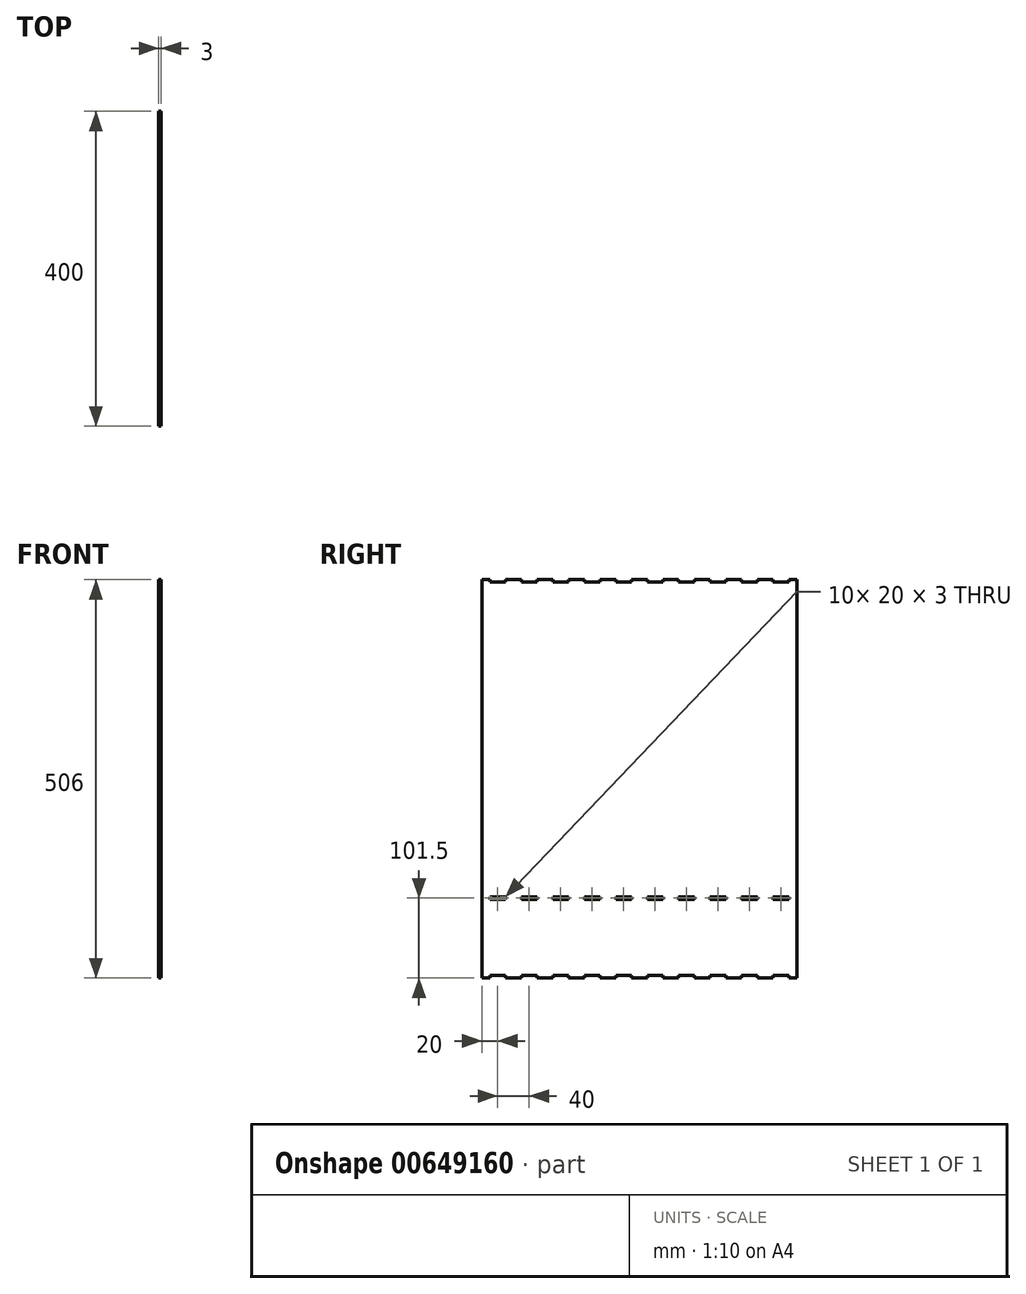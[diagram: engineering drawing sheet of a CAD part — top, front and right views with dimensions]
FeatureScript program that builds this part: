
annotation { "Feature Type Name" : "Feature", "Feature Type Description" : "" }
export const myFeature = defineFeature(function(context is Context, id is Id, definition is map)
    precondition{}
    {
        {
            var Q0;
            Q0=qCreatedBy(makeId("Right.planeOp"),FACE);
            var sketch = newSketch(context, id + "F0", { "sketchPlane" : qUnion([Q0])});
            skLineSegment(sketch, "E0.bottom", {"start": v(200, 250) * mm, "end": v(-200, 250) * mm});
            skLineSegment(sketch, "E0.top", {"start": v(200, -250) * mm, "end": v(-200, -250) * mm});
            skLineSegment(sketch, "E0.left", {"start": v(200, 250) * mm, "end": v(200, -250) * mm});
            skLineSegment(sketch, "E0.right", {"start": v(-200, 250) * mm, "end": v(-200, -250) * mm});
            skPoint(sketch, "E0.middle", {"position": v(0, 0) * mm});
            skSolve(sketch);
        }
        {
            var Q0;
            Q0=qSketchRegion(id+"F0",true);
            extrude(context, id + "F1", {"entities" : qUnion([Q0]), "depth" : 3 * mm, "offsetDistance" : 25 * mm});
        }
        {
            var Q0;
            Q0=makeQuery(id+"F1.opExtrude","CAP_FACE",FACE,{"disambiguationData":[OSD([sQuery(id+"F0.wireOp",EDGE,"E0.bottom"),sQuery(id+"F0.wireOp",EDGE,"E0.top"),sQuery(id+"F0.wireOp",EDGE,"E0.left"),sQuery(id+"F0.wireOp",EDGE,"E0.right")])],"isStart":false});
            var sketch = newSketch(context, id + "F2", { "sketchPlane" : qUnion([Q0])});
            skLineSegment(sketch, "E1.bottom", {"start": v(-200, 250) * mm, "end": v(-190, 250) * mm});
            skLineSegment(sketch, "E1.top", {"start": v(-200, 253) * mm, "end": v(-190, 253) * mm});
            skLineSegment(sketch, "E1.left", {"start": v(-200, 250) * mm, "end": v(-200, 253) * mm});
            skLineSegment(sketch, "E1.right", {"start": v(-190, 250) * mm, "end": v(-190, 253) * mm});
            skLineSegment(sketch, "E2", {"start": v(-190, 250) * mm, "end": v(-170, 250) * mm, "construction": true});
            skLineSegment(sketch, "E3.bottom", {"start": v(-170, 250) * mm, "end": v(-150, 250) * mm});
            skLineSegment(sketch, "E3.top", {"start": v(-170, 253) * mm, "end": v(-150, 253) * mm});
            skLineSegment(sketch, "E3.left", {"start": v(-170, 250) * mm, "end": v(-170, 253) * mm});
            skLineSegment(sketch, "E3.right", {"start": v(-150, 250) * mm, "end": v(-150, 253) * mm});
            skLineSegment(sketch, "E4.1.0.0", {"start": v(-110, 250) * mm, "end": v(-110, 253) * mm});
            skLineSegment(sketch, "E4.1.0.1", {"start": v(-130, 250) * mm, "end": v(-110, 250) * mm});
            skLineSegment(sketch, "E4.1.0.2", {"start": v(-130, 250) * mm, "end": v(-130, 253) * mm});
            skLineSegment(sketch, "E4.1.0.3", {"start": v(-130, 253) * mm, "end": v(-110, 253) * mm});
            skLineSegment(sketch, "E4.2.0.0", {"start": v(-70, 250) * mm, "end": v(-70, 253) * mm});
            skLineSegment(sketch, "E4.2.0.1", {"start": v(-90, 250) * mm, "end": v(-70, 250) * mm});
            skLineSegment(sketch, "E4.2.0.2", {"start": v(-90, 250) * mm, "end": v(-90, 253) * mm});
            skLineSegment(sketch, "E4.2.0.3", {"start": v(-90, 253) * mm, "end": v(-70, 253) * mm});
            skLineSegment(sketch, "E4.3.0.0", {"start": v(-30, 250) * mm, "end": v(-30, 253) * mm});
            skLineSegment(sketch, "E4.3.0.1", {"start": v(-50, 250) * mm, "end": v(-30, 250) * mm});
            skLineSegment(sketch, "E4.3.0.2", {"start": v(-50, 250) * mm, "end": v(-50, 253) * mm});
            skLineSegment(sketch, "E4.3.0.3", {"start": v(-50, 253) * mm, "end": v(-30, 253) * mm});
            skLineSegment(sketch, "E4.4.0.0", {"start": v(10, 250) * mm, "end": v(10, 253) * mm});
            skLineSegment(sketch, "E4.4.0.1", {"start": v(-10, 250) * mm, "end": v(10, 250) * mm});
            skLineSegment(sketch, "E4.4.0.2", {"start": v(-10, 250) * mm, "end": v(-10, 253) * mm});
            skLineSegment(sketch, "E4.4.0.3", {"start": v(-10, 253) * mm, "end": v(10, 253) * mm});
            skLineSegment(sketch, "E4.5.0.0", {"start": v(50, 250) * mm, "end": v(50, 253) * mm});
            skLineSegment(sketch, "E4.5.0.1", {"start": v(30, 250) * mm, "end": v(50, 250) * mm});
            skLineSegment(sketch, "E4.5.0.2", {"start": v(30, 250) * mm, "end": v(30, 253) * mm});
            skLineSegment(sketch, "E4.5.0.3", {"start": v(30, 253) * mm, "end": v(50, 253) * mm});
            skLineSegment(sketch, "E4.6.0.0", {"start": v(90, 250) * mm, "end": v(90, 253) * mm});
            skLineSegment(sketch, "E4.6.0.1", {"start": v(70, 250) * mm, "end": v(90, 250) * mm});
            skLineSegment(sketch, "E4.6.0.2", {"start": v(70, 250) * mm, "end": v(70, 253) * mm});
            skLineSegment(sketch, "E4.6.0.3", {"start": v(70, 253) * mm, "end": v(90, 253) * mm});
            skLineSegment(sketch, "E4.7.0.0", {"start": v(130, 250) * mm, "end": v(130, 253) * mm});
            skLineSegment(sketch, "E4.7.0.1", {"start": v(110, 250) * mm, "end": v(130, 250) * mm});
            skLineSegment(sketch, "E4.7.0.2", {"start": v(110, 250) * mm, "end": v(110, 253) * mm});
            skLineSegment(sketch, "E4.7.0.3", {"start": v(110, 253) * mm, "end": v(130, 253) * mm});
            skLineSegment(sketch, "E4.8.0.0", {"start": v(170, 250) * mm, "end": v(170, 253) * mm});
            skLineSegment(sketch, "E4.8.0.1", {"start": v(150, 250) * mm, "end": v(170, 250) * mm});
            skLineSegment(sketch, "E4.8.0.2", {"start": v(150, 250) * mm, "end": v(150, 253) * mm});
            skLineSegment(sketch, "E4.8.0.3", {"start": v(150, 253) * mm, "end": v(170, 253) * mm});
            skLineSegment(sketch, "E4.direction1", {"start": v(-170, 250) * mm, "end": v(-130, 250) * mm, "construction": true});
            skLineSegment(sketch, "E5.bottom", {"start": v(200, 250) * mm, "end": v(190, 250) * mm});
            skLineSegment(sketch, "E5.top", {"start": v(200, 253) * mm, "end": v(190, 253) * mm});
            skLineSegment(sketch, "E5.left", {"start": v(200, 250) * mm, "end": v(200, 253) * mm});
            skLineSegment(sketch, "E5.right", {"start": v(190, 250) * mm, "end": v(190, 253) * mm});
            skLineSegment(sketch, "E6.MirrorCS", {"start": v(-110, -250) * mm, "end": v(-110, -253) * mm});
            skLineSegment(sketch, "E7.MirrorCS", {"start": v(-170, -250) * mm, "end": v(-150, -250) * mm});
            skLineSegment(sketch, "E8.MirrorCS", {"start": v(-90, -253) * mm, "end": v(-70, -253) * mm});
            skLineSegment(sketch, "E9.MirrorCS", {"start": v(10, -250) * mm, "end": v(10, -253) * mm});
            skLineSegment(sketch, "E10.MirrorCS", {"start": v(170, -250) * mm, "end": v(170, -253) * mm});
            skLineSegment(sketch, "E11.MirrorCS", {"start": v(90, -250) * mm, "end": v(90, -253) * mm});
            skLineSegment(sketch, "E12.MirrorCS", {"start": v(200, -253) * mm, "end": v(190, -253) * mm});
            skLineSegment(sketch, "E13.MirrorCS", {"start": v(200, -250) * mm, "end": v(190, -250) * mm});
            skLineSegment(sketch, "E14.MirrorCS", {"start": v(-130, -253) * mm, "end": v(-110, -253) * mm});
            skLineSegment(sketch, "E15.MirrorCS", {"start": v(50, -250) * mm, "end": v(50, -253) * mm});
            skLineSegment(sketch, "E16.MirrorCS", {"start": v(-130, -250) * mm, "end": v(-130, -253) * mm});
            skLineSegment(sketch, "E17.MirrorCS", {"start": v(-130, -250) * mm, "end": v(-110, -250) * mm});
            skLineSegment(sketch, "E18.MirrorCS", {"start": v(-150, -250) * mm, "end": v(-150, -253) * mm});
            skLineSegment(sketch, "E19.MirrorCS", {"start": v(-170, -250) * mm, "end": v(-170, -253) * mm});
            skLineSegment(sketch, "E20.MirrorCS", {"start": v(-170, -253) * mm, "end": v(-150, -253) * mm});
            skLineSegment(sketch, "E21.MirrorCS", {"start": v(-190, -250) * mm, "end": v(-170, -250) * mm, "construction": true});
            skLineSegment(sketch, "E22.MirrorCS", {"start": v(-190, -250) * mm, "end": v(-190, -253) * mm});
            skLineSegment(sketch, "E23.MirrorCS", {"start": v(-200, -253) * mm, "end": v(-190, -253) * mm});
            skLineSegment(sketch, "E24.MirrorCS", {"start": v(-200, -250) * mm, "end": v(-190, -250) * mm});
            skLineSegment(sketch, "E25.MirrorCS", {"start": v(-90, -250) * mm, "end": v(-90, -253) * mm});
            skLineSegment(sketch, "E26.MirrorCS", {"start": v(-90, -250) * mm, "end": v(-70, -250) * mm});
            skLineSegment(sketch, "E27.MirrorCS", {"start": v(-70, -250) * mm, "end": v(-70, -253) * mm});
            skLineSegment(sketch, "E28.MirrorCS", {"start": v(-30, -250) * mm, "end": v(-30, -253) * mm});
            skLineSegment(sketch, "E29.MirrorCS", {"start": v(130, -250) * mm, "end": v(130, -253) * mm});
            skLineSegment(sketch, "E30.MirrorCS", {"start": v(-10, -253) * mm, "end": v(10, -253) * mm});
            skLineSegment(sketch, "E31.MirrorCS", {"start": v(150, -253) * mm, "end": v(170, -253) * mm});
            skLineSegment(sketch, "E32.MirrorCS", {"start": v(70, -253) * mm, "end": v(90, -253) * mm});
            skLineSegment(sketch, "E33.MirrorCS", {"start": v(-10, -250) * mm, "end": v(-10, -253) * mm});
            skLineSegment(sketch, "E34.MirrorCS", {"start": v(150, -250) * mm, "end": v(150, -253) * mm});
            skLineSegment(sketch, "E35.MirrorCS", {"start": v(-10, -250) * mm, "end": v(10, -250) * mm});
            skLineSegment(sketch, "E36.MirrorCS", {"start": v(70, -250) * mm, "end": v(70, -253) * mm});
            skLineSegment(sketch, "E37.MirrorCS", {"start": v(150, -250) * mm, "end": v(170, -250) * mm});
            skLineSegment(sketch, "E38.MirrorCS", {"start": v(70, -250) * mm, "end": v(90, -250) * mm});
            skLineSegment(sketch, "E39.MirrorCS", {"start": v(200, -250) * mm, "end": v(200, -253) * mm});
            skLineSegment(sketch, "E40.MirrorCS", {"start": v(190, -250) * mm, "end": v(190, -253) * mm});
            skLineSegment(sketch, "E41.MirrorCS", {"start": v(-50, -253) * mm, "end": v(-30, -253) * mm});
            skLineSegment(sketch, "E42.MirrorCS", {"start": v(110, -253) * mm, "end": v(130, -253) * mm});
            skLineSegment(sketch, "E43.MirrorCS", {"start": v(30, -250) * mm, "end": v(30, -253) * mm});
            skLineSegment(sketch, "E44.MirrorCS", {"start": v(-50, -250) * mm, "end": v(-50, -253) * mm});
            skLineSegment(sketch, "E45.MirrorCS", {"start": v(110, -250) * mm, "end": v(110, -253) * mm});
            skLineSegment(sketch, "E46.MirrorCS", {"start": v(30, -250) * mm, "end": v(50, -250) * mm});
            skLineSegment(sketch, "E47.MirrorCS", {"start": v(-50, -250) * mm, "end": v(-30, -250) * mm});
            skLineSegment(sketch, "E48.MirrorCS", {"start": v(110, -250) * mm, "end": v(130, -250) * mm});
            skLineSegment(sketch, "E49.MirrorCS", {"start": v(-170, -250) * mm, "end": v(-130, -250) * mm, "construction": true});
            skLineSegment(sketch, "E50.MirrorCS", {"start": v(-200, -250) * mm, "end": v(-200, -253) * mm});
            skLineSegment(sketch, "E51.MirrorCS", {"start": v(30, -253) * mm, "end": v(50, -253) * mm});
            skSolve(sketch);
        }
        {
            var Q0;
            Q0=qSketchRegion(id+"F2",true);
            var Q1;
            Q1=makeQuery(id+"F1.opExtrude","CAP_FACE",FACE,{"disambiguationData":[OSD([sQuery(id+"F0.wireOp",EDGE,"E0.bottom"),sQuery(id+"F0.wireOp",EDGE,"E0.top"),sQuery(id+"F0.wireOp",EDGE,"E0.left"),sQuery(id+"F0.wireOp",EDGE,"E0.right")])],"isStart":true});
            extrude(context, id + "F3", {"entities" : qUnion([Q0]), "operationType" : NewBodyOperationType.ADD, "endBound" : BoundingType.UP_TO_SURFACE, "oppositeDirection" : true, "depth" : 25 * mm, "endBoundEntityFace" : qUnion([Q1]), "offsetDistance" : 25 * mm});
        }
        {
            var Q0;
            Q0=makeQuery(id+"F3.boolean.opBoolean","MERGE",FACE,{"derivedFrom":[makeQuery(id+"F1.opExtrude","CAP_FACE",FACE,{"disambiguationData":[OSD([sQuery(id+"F0.wireOp",EDGE,"E0.bottom"),sQuery(id+"F0.wireOp",EDGE,"E0.top"),sQuery(id+"F0.wireOp",EDGE,"E0.left"),sQuery(id+"F0.wireOp",EDGE,"E0.right")])],"isStart":false}),makeQuery(id+"F3.opExtrude","CAP_FACE",FACE,{"disambiguationData":[OSD([sQuery(id+"F2.wireOp",EDGE,"E1.bottom"),sQuery(id+"F2.wireOp",EDGE,"E1.top"),sQuery(id+"F2.wireOp",EDGE,"E1.left"),sQuery(id+"F2.wireOp",EDGE,"E1.right")])],"isStart":true}),makeQuery(id+"F3.opExtrude","CAP_FACE",FACE,{"disambiguationData":[OSD([sQuery(id+"F2.wireOp",EDGE,"E3.bottom"),sQuery(id+"F2.wireOp",EDGE,"E3.top"),sQuery(id+"F2.wireOp",EDGE,"E3.left"),sQuery(id+"F2.wireOp",EDGE,"E3.right")])],"isStart":true}),makeQuery(id+"F3.opExtrude","CAP_FACE",FACE,{"disambiguationData":[OSD([sQuery(id+"F2.wireOp",EDGE,"E4.1.0.0"),sQuery(id+"F2.wireOp",EDGE,"E4.1.0.1"),sQuery(id+"F2.wireOp",EDGE,"E4.1.0.2"),sQuery(id+"F2.wireOp",EDGE,"E4.1.0.3")])],"isStart":true}),makeQuery(id+"F3.opExtrude","CAP_FACE",FACE,{"disambiguationData":[OSD([sQuery(id+"F2.wireOp",EDGE,"E4.2.0.0"),sQuery(id+"F2.wireOp",EDGE,"E4.2.0.1"),sQuery(id+"F2.wireOp",EDGE,"E4.2.0.2"),sQuery(id+"F2.wireOp",EDGE,"E4.2.0.3")])],"isStart":true}),makeQuery(id+"F3.opExtrude","CAP_FACE",FACE,{"disambiguationData":[OSD([sQuery(id+"F2.wireOp",EDGE,"E4.3.0.0"),sQuery(id+"F2.wireOp",EDGE,"E4.3.0.1"),sQuery(id+"F2.wireOp",EDGE,"E4.3.0.2"),sQuery(id+"F2.wireOp",EDGE,"E4.3.0.3")])],"isStart":true}),makeQuery(id+"F3.opExtrude","CAP_FACE",FACE,{"disambiguationData":[OSD([sQuery(id+"F2.wireOp",EDGE,"E4.4.0.0"),sQuery(id+"F2.wireOp",EDGE,"E4.4.0.1"),sQuery(id+"F2.wireOp",EDGE,"E4.4.0.2"),sQuery(id+"F2.wireOp",EDGE,"E4.4.0.3")])],"isStart":true}),makeQuery(id+"F3.opExtrude","CAP_FACE",FACE,{"disambiguationData":[OSD([sQuery(id+"F2.wireOp",EDGE,"E4.5.0.0"),sQuery(id+"F2.wireOp",EDGE,"E4.5.0.1"),sQuery(id+"F2.wireOp",EDGE,"E4.5.0.2"),sQuery(id+"F2.wireOp",EDGE,"E4.5.0.3")])],"isStart":true}),makeQuery(id+"F3.opExtrude","CAP_FACE",FACE,{"disambiguationData":[OSD([sQuery(id+"F2.wireOp",EDGE,"E4.6.0.0"),sQuery(id+"F2.wireOp",EDGE,"E4.6.0.1"),sQuery(id+"F2.wireOp",EDGE,"E4.6.0.2"),sQuery(id+"F2.wireOp",EDGE,"E4.6.0.3")])],"isStart":true}),makeQuery(id+"F3.opExtrude","CAP_FACE",FACE,{"disambiguationData":[OSD([sQuery(id+"F2.wireOp",EDGE,"E4.7.0.0"),sQuery(id+"F2.wireOp",EDGE,"E4.7.0.1"),sQuery(id+"F2.wireOp",EDGE,"E4.7.0.2"),sQuery(id+"F2.wireOp",EDGE,"E4.7.0.3")])],"isStart":true}),makeQuery(id+"F3.opExtrude","CAP_FACE",FACE,{"disambiguationData":[OSD([sQuery(id+"F2.wireOp",EDGE,"E4.8.0.0"),sQuery(id+"F2.wireOp",EDGE,"E4.8.0.1"),sQuery(id+"F2.wireOp",EDGE,"E4.8.0.2"),sQuery(id+"F2.wireOp",EDGE,"E4.8.0.3")])],"isStart":true}),makeQuery(id+"F3.opExtrude","CAP_FACE",FACE,{"disambiguationData":[OSD([sQuery(id+"F2.wireOp",EDGE,"E5.bottom"),sQuery(id+"F2.wireOp",EDGE,"E5.top"),sQuery(id+"F2.wireOp",EDGE,"E5.left"),sQuery(id+"F2.wireOp",EDGE,"E5.right")])],"isStart":true}),makeQuery(id+"F3.opExtrude","CAP_FACE",FACE,{"disambiguationData":[OSD([sQuery(id+"F2.wireOp",EDGE,"E6.MirrorCS"),sQuery(id+"F2.wireOp",EDGE,"E14.MirrorCS"),sQuery(id+"F2.wireOp",EDGE,"E16.MirrorCS"),sQuery(id+"F2.wireOp",EDGE,"E17.MirrorCS")])],"isStart":true}),makeQuery(id+"F3.opExtrude","CAP_FACE",FACE,{"disambiguationData":[OSD([sQuery(id+"F2.wireOp",EDGE,"E7.MirrorCS"),sQuery(id+"F2.wireOp",EDGE,"E18.MirrorCS"),sQuery(id+"F2.wireOp",EDGE,"E19.MirrorCS"),sQuery(id+"F2.wireOp",EDGE,"E20.MirrorCS")])],"isStart":true}),makeQuery(id+"F3.opExtrude","CAP_FACE",FACE,{"disambiguationData":[OSD([sQuery(id+"F2.wireOp",EDGE,"E8.MirrorCS"),sQuery(id+"F2.wireOp",EDGE,"E25.MirrorCS"),sQuery(id+"F2.wireOp",EDGE,"E26.MirrorCS"),sQuery(id+"F2.wireOp",EDGE,"E27.MirrorCS")])],"isStart":true}),makeQuery(id+"F3.opExtrude","CAP_FACE",FACE,{"disambiguationData":[OSD([sQuery(id+"F2.wireOp",EDGE,"E9.MirrorCS"),sQuery(id+"F2.wireOp",EDGE,"E30.MirrorCS"),sQuery(id+"F2.wireOp",EDGE,"E33.MirrorCS"),sQuery(id+"F2.wireOp",EDGE,"E35.MirrorCS")])],"isStart":true}),makeQuery(id+"F3.opExtrude","CAP_FACE",FACE,{"disambiguationData":[OSD([sQuery(id+"F2.wireOp",EDGE,"E10.MirrorCS"),sQuery(id+"F2.wireOp",EDGE,"E31.MirrorCS"),sQuery(id+"F2.wireOp",EDGE,"E34.MirrorCS"),sQuery(id+"F2.wireOp",EDGE,"E37.MirrorCS")])],"isStart":true}),makeQuery(id+"F3.opExtrude","CAP_FACE",FACE,{"disambiguationData":[OSD([sQuery(id+"F2.wireOp",EDGE,"E11.MirrorCS"),sQuery(id+"F2.wireOp",EDGE,"E32.MirrorCS"),sQuery(id+"F2.wireOp",EDGE,"E36.MirrorCS"),sQuery(id+"F2.wireOp",EDGE,"E38.MirrorCS")])],"isStart":true}),makeQuery(id+"F3.opExtrude","CAP_FACE",FACE,{"disambiguationData":[OSD([sQuery(id+"F2.wireOp",EDGE,"E12.MirrorCS"),sQuery(id+"F2.wireOp",EDGE,"E13.MirrorCS"),sQuery(id+"F2.wireOp",EDGE,"E39.MirrorCS"),sQuery(id+"F2.wireOp",EDGE,"E40.MirrorCS")])],"isStart":true}),makeQuery(id+"F3.opExtrude","CAP_FACE",FACE,{"disambiguationData":[OSD([sQuery(id+"F2.wireOp",EDGE,"E15.MirrorCS"),sQuery(id+"F2.wireOp",EDGE,"E43.MirrorCS"),sQuery(id+"F2.wireOp",EDGE,"E46.MirrorCS"),sQuery(id+"F2.wireOp",EDGE,"E51.MirrorCS")])],"isStart":true}),makeQuery(id+"F3.opExtrude","CAP_FACE",FACE,{"disambiguationData":[OSD([sQuery(id+"F2.wireOp",EDGE,"E22.MirrorCS"),sQuery(id+"F2.wireOp",EDGE,"E23.MirrorCS"),sQuery(id+"F2.wireOp",EDGE,"E24.MirrorCS"),sQuery(id+"F2.wireOp",EDGE,"E50.MirrorCS")])],"isStart":true}),makeQuery(id+"F3.opExtrude","CAP_FACE",FACE,{"disambiguationData":[OSD([sQuery(id+"F2.wireOp",EDGE,"E28.MirrorCS"),sQuery(id+"F2.wireOp",EDGE,"E41.MirrorCS"),sQuery(id+"F2.wireOp",EDGE,"E44.MirrorCS"),sQuery(id+"F2.wireOp",EDGE,"E47.MirrorCS")])],"isStart":true}),makeQuery(id+"F3.opExtrude","CAP_FACE",FACE,{"disambiguationData":[OSD([sQuery(id+"F2.wireOp",EDGE,"E29.MirrorCS"),sQuery(id+"F2.wireOp",EDGE,"E42.MirrorCS"),sQuery(id+"F2.wireOp",EDGE,"E45.MirrorCS"),sQuery(id+"F2.wireOp",EDGE,"E48.MirrorCS")])],"isStart":true})]});
            var sketch = newSketch(context, id + "F4", { "sketchPlane" : qUnion([Q0])});
            skLineSegment(sketch, "E52", {"start": v(-200, 253) * mm, "end": v(-200, -153) * mm, "construction": true});
            skLineSegment(sketch, "E53", {"start": v(-200, -153) * mm, "end": v(-190, -153) * mm, "construction": true});
            skLineSegment(sketch, "E54.bottom", {"start": v(-190, -153) * mm, "end": v(-170, -153) * mm});
            skLineSegment(sketch, "E54.top", {"start": v(-190, -150) * mm, "end": v(-170, -150) * mm});
            skLineSegment(sketch, "E54.left", {"start": v(-190, -153) * mm, "end": v(-190, -150) * mm});
            skLineSegment(sketch, "E54.right", {"start": v(-170, -153) * mm, "end": v(-170, -150) * mm});
            skLineSegment(sketch, "E55.1.0.0", {"start": v(-150, -153) * mm, "end": v(-150, -150) * mm});
            skLineSegment(sketch, "E55.1.0.1", {"start": v(-150, -153) * mm, "end": v(-130, -153) * mm});
            skLineSegment(sketch, "E55.1.0.2", {"start": v(-130, -153) * mm, "end": v(-130, -150) * mm});
            skLineSegment(sketch, "E55.1.0.3", {"start": v(-150, -150) * mm, "end": v(-130, -150) * mm});
            skLineSegment(sketch, "E55.2.0.0", {"start": v(-110, -153) * mm, "end": v(-110, -150) * mm});
            skLineSegment(sketch, "E55.2.0.1", {"start": v(-110, -153) * mm, "end": v(-90, -153) * mm});
            skLineSegment(sketch, "E55.2.0.2", {"start": v(-90, -153) * mm, "end": v(-90, -150) * mm});
            skLineSegment(sketch, "E55.2.0.3", {"start": v(-110, -150) * mm, "end": v(-90, -150) * mm});
            skLineSegment(sketch, "E55.3.0.0", {"start": v(-70, -153) * mm, "end": v(-70, -150) * mm});
            skLineSegment(sketch, "E55.3.0.1", {"start": v(-70, -153) * mm, "end": v(-50, -153) * mm});
            skLineSegment(sketch, "E55.3.0.2", {"start": v(-50, -153) * mm, "end": v(-50, -150) * mm});
            skLineSegment(sketch, "E55.3.0.3", {"start": v(-70, -150) * mm, "end": v(-50, -150) * mm});
            skLineSegment(sketch, "E55.4.0.0", {"start": v(-30, -153) * mm, "end": v(-30, -150) * mm});
            skLineSegment(sketch, "E55.4.0.1", {"start": v(-30, -153) * mm, "end": v(-10, -153) * mm});
            skLineSegment(sketch, "E55.4.0.2", {"start": v(-10, -153) * mm, "end": v(-10, -150) * mm});
            skLineSegment(sketch, "E55.4.0.3", {"start": v(-30, -150) * mm, "end": v(-10, -150) * mm});
            skLineSegment(sketch, "E55.5.0.0", {"start": v(10, -153) * mm, "end": v(10, -150) * mm});
            skLineSegment(sketch, "E55.5.0.1", {"start": v(10, -153) * mm, "end": v(30, -153) * mm});
            skLineSegment(sketch, "E55.5.0.2", {"start": v(30, -153) * mm, "end": v(30, -150) * mm});
            skLineSegment(sketch, "E55.5.0.3", {"start": v(10, -150) * mm, "end": v(30, -150) * mm});
            skLineSegment(sketch, "E55.6.0.0", {"start": v(50, -153) * mm, "end": v(50, -150) * mm});
            skLineSegment(sketch, "E55.6.0.1", {"start": v(50, -153) * mm, "end": v(70, -153) * mm});
            skLineSegment(sketch, "E55.6.0.2", {"start": v(70, -153) * mm, "end": v(70, -150) * mm});
            skLineSegment(sketch, "E55.6.0.3", {"start": v(50, -150) * mm, "end": v(70, -150) * mm});
            skLineSegment(sketch, "E55.7.0.0", {"start": v(90, -153) * mm, "end": v(90, -150) * mm});
            skLineSegment(sketch, "E55.7.0.1", {"start": v(90, -153) * mm, "end": v(110, -153) * mm});
            skLineSegment(sketch, "E55.7.0.2", {"start": v(110, -153) * mm, "end": v(110, -150) * mm});
            skLineSegment(sketch, "E55.7.0.3", {"start": v(90, -150) * mm, "end": v(110, -150) * mm});
            skLineSegment(sketch, "E55.8.0.0", {"start": v(130, -153) * mm, "end": v(130, -150) * mm});
            skLineSegment(sketch, "E55.8.0.1", {"start": v(130, -153) * mm, "end": v(150, -153) * mm});
            skLineSegment(sketch, "E55.8.0.2", {"start": v(150, -153) * mm, "end": v(150, -150) * mm});
            skLineSegment(sketch, "E55.8.0.3", {"start": v(130, -150) * mm, "end": v(150, -150) * mm});
            skLineSegment(sketch, "E55.9.0.0", {"start": v(170, -153) * mm, "end": v(170, -150) * mm});
            skLineSegment(sketch, "E55.9.0.1", {"start": v(170, -153) * mm, "end": v(190, -153) * mm});
            skLineSegment(sketch, "E55.9.0.2", {"start": v(190, -153) * mm, "end": v(190, -150) * mm});
            skLineSegment(sketch, "E55.9.0.3", {"start": v(170, -150) * mm, "end": v(190, -150) * mm});
            skLineSegment(sketch, "E55.direction1", {"start": v(-190, -153) * mm, "end": v(-150, -153) * mm, "construction": true});
            skSolve(sketch);
        }
        {
            var Q0;
            Q0 = qSketchRegion(id + "F4", true);
            extrude(context, id + "F5", {"entities" : qUnion([Q0]), "operationType" : NewBodyOperationType.REMOVE, "oppositeDirection" : true, "depth" : 25 * mm, "offsetDistance" : 25 * mm});
        }
    });
